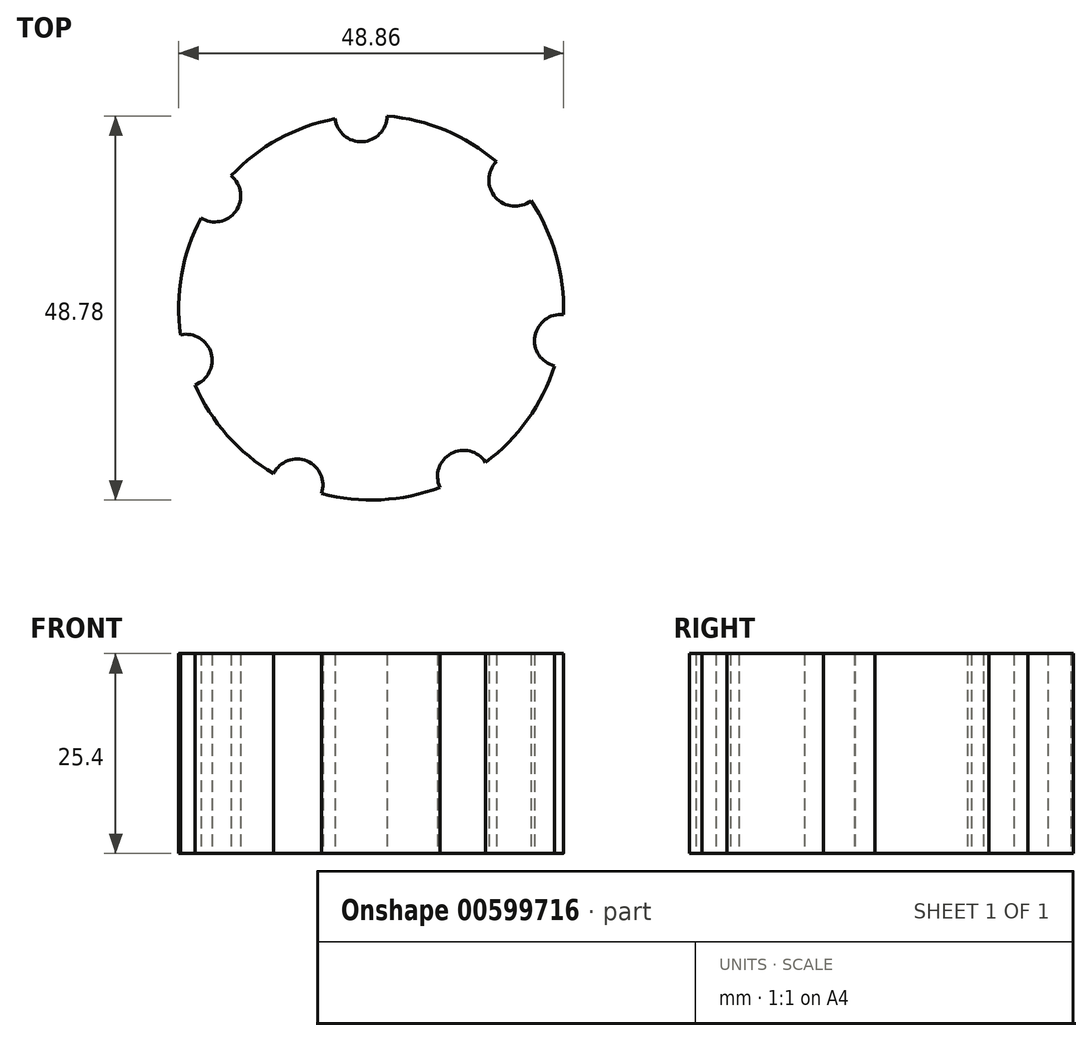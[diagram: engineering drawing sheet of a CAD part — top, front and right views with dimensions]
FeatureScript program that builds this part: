
annotation { "Feature Type Name" : "Feature", "Feature Type Description" : "" }
export const myFeature = defineFeature(function(context is Context, id is Id, definition is map)
    precondition{}
    {
        {
            var Q0;
            Q0=qCreatedBy(makeId("Top.planeOp"),FACE);
            var sketch = newSketch(context, id + "F0", { "sketchPlane" : qUnion([Q0])});
            skCircle(sketch, "E0", {"center": v(0, 0) * mm, "radius": 24.43 * mm});
            skSolve(sketch);
        }
        {
            var Q0;
            Q0 = qSketchRegion(id + "F0", true);
            extrude(context, id + "F1", {"entities" : qUnion([Q0]), "depth" : 25.4 * mm, "offsetDistance" : 25.4 * mm});
        }
        {
            var Q0;
            Q0=makeQuery(id+"F1.opExtrude","CAP_FACE",FACE,{"disambiguationData":[OSD([sQuery(id+"F0.wireOp",EDGE,"E0")])],"isStart":false});
            var sketch = newSketch(context, id + "F2", { "sketchPlane" : qUnion([Q0])});
            skCircle(sketch, "E1", {"center": v(-9.43, -22.54) * mm, "radius": 3.31 * mm});
            skSolve(sketch);
        }
        {
            var Q0;
            Q0 = qSketchRegion(id + "F2", true);
            extrude(context, id + "F3", {"entities" : qUnion([Q0]), "depth" : 5.84 * mm, "offsetDistance" : 25.4 * mm, "hasSecondDirection" : true, "secondDirectionOppositeDirection" : true, "secondDirectionDepth" : 30.99 * mm});
        }
        {
            var Q0;
            Q0=makeQuery(id+"F3.opExtrude","SWEPT_BODY",BODY,{"disambiguationData":[OSD([sQuery(id+"F2.wireOp",EDGE,"E1")])]});
            var Q1;
            Q1=makeQuery(id+"F1.opExtrude","CAP_EDGE",EDGE,{"disambiguationData":[OSD([sQuery(id+"F0.wireOp",EDGE,"E0")])],"isStart":false});
            circularPattern(context, id + "F4", {"entities" : qUnion([Q0]), "axis" : qUnion([Q1]), "angle" : 360 * degree, "instanceCount" : 7, "equalSpace" : true});
        }
        {
            var Q0;
            Q0=makeQuery(id+"F3.opExtrude","SWEPT_BODY",BODY,{"disambiguationData":[OSD([sQuery(id+"F2.wireOp",EDGE,"E1")])]});
            var Q1;
            Q1=makeQuery(id+"F4.opPattern","COPY",BODY,{"derivedFrom":makeQuery(id+"F3.opExtrude","SWEPT_BODY",BODY,{"disambiguationData":[OSD([sQuery(id+"F2.wireOp",EDGE,"E1")])]}),"instanceName":"1"});
            var Q2;
            Q2=makeQuery(id+"F4.opPattern","COPY",BODY,{"derivedFrom":makeQuery(id+"F3.opExtrude","SWEPT_BODY",BODY,{"disambiguationData":[OSD([sQuery(id+"F2.wireOp",EDGE,"E1")])]}),"instanceName":"2"});
            var Q3;
            Q3=makeQuery(id+"F4.opPattern","COPY",BODY,{"derivedFrom":makeQuery(id+"F3.opExtrude","SWEPT_BODY",BODY,{"disambiguationData":[OSD([sQuery(id+"F2.wireOp",EDGE,"E1")])]}),"instanceName":"3"});
            var Q4;
            Q4=makeQuery(id+"F4.opPattern","COPY",BODY,{"derivedFrom":makeQuery(id+"F3.opExtrude","SWEPT_BODY",BODY,{"disambiguationData":[OSD([sQuery(id+"F2.wireOp",EDGE,"E1")])]}),"instanceName":"4"});
            var Q5;
            Q5=makeQuery(id+"F4.opPattern","COPY",BODY,{"derivedFrom":makeQuery(id+"F3.opExtrude","SWEPT_BODY",BODY,{"disambiguationData":[OSD([sQuery(id+"F2.wireOp",EDGE,"E1")])]}),"instanceName":"5"});
            var Q6;
            Q6=makeQuery(id+"F4.opPattern","COPY",BODY,{"derivedFrom":makeQuery(id+"F3.opExtrude","SWEPT_BODY",BODY,{"disambiguationData":[OSD([sQuery(id+"F2.wireOp",EDGE,"E1")])]}),"instanceName":"6"});
            var Q7;
            Q7=makeQuery(id+"F1.opExtrude","SWEPT_BODY",BODY,{"disambiguationData":[OSD([sQuery(id+"F0.wireOp",EDGE,"E0")])]});
            booleanBodies(context, id + "F5", {"operationType" : BooleanOperationType.SUBTRACTION, "tools" : qUnion([Q0, Q1, Q2, Q3, Q4, Q5, Q6]), "targets" : qUnion([Q7])});
        }
    });
